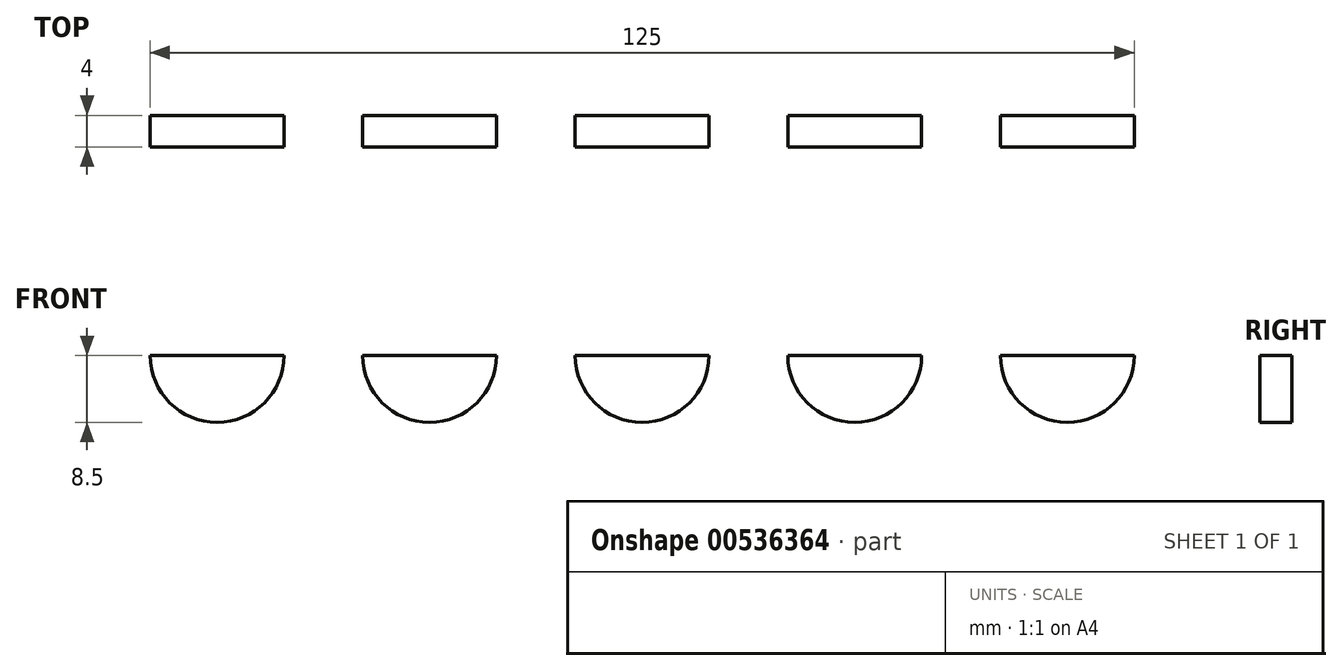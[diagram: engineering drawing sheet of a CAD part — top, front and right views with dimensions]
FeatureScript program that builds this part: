
annotation { "Feature Type Name" : "Feature", "Feature Type Description" : "" }
export const myFeature = defineFeature(function(context is Context, id is Id, definition is map)
    precondition{}
    {
        {
            var Q0;
            Q0=qCreatedBy(makeId("Front.planeOp"),FACE);
            var sketch = newSketch(context, id + "F0", { "sketchPlane" : qUnion([Q0])});
            skLineSegment(sketch, "E0.bottom", {"start": v(-72.5, 7.5) * mm, "end": v(72.5, 7.5) * mm});
            skLineSegment(sketch, "E0.top", {"start": v(-72.5, -7.5) * mm, "end": v(72.5, -7.5) * mm});
            skLineSegment(sketch, "E0.left", {"start": v(-72.5, 7.5) * mm, "end": v(-72.5, -7.5) * mm});
            skLineSegment(sketch, "E0.right", {"start": v(72.5, 7.5) * mm, "end": v(72.5, -7.5) * mm});
            skPoint(sketch, "E0.middle", {"position": v(0, 0) * mm});
            skLineSegment(sketch, "E1", {"start": v(-72.5, 7.5) * mm, "end": v(-62.5, 7.5) * mm});
            skLineSegment(sketch, "E2", {"start": v(-62.5, 7.5) * mm, "end": v(-54, 7.5) * mm});
            skLineSegment(sketch, "E3", {"start": v(-54, 7.5) * mm, "end": v(-45.5, 7.5) * mm});
            skLineSegment(sketch, "E4", {"start": v(-45.5, 7.5) * mm, "end": v(-35.5, 7.5) * mm});
            skLineSegment(sketch, "E5", {"start": v(-35.5, 7.5) * mm, "end": v(-27, 7.5) * mm});
            skLineSegment(sketch, "E6", {"start": v(-27, 7.5) * mm, "end": v(-18.5, 7.5) * mm});
            skLineSegment(sketch, "E7", {"start": v(-18.5, 7.5) * mm, "end": v(-8.5, 7.5) * mm});
            skLineSegment(sketch, "E8", {"start": v(-8.5, 7.5) * mm, "end": v(0, 7.5) * mm});
            skLineSegment(sketch, "E9", {"start": v(0, 7.5) * mm, "end": v(8.5, 7.5) * mm});
            skLineSegment(sketch, "E10", {"start": v(8.5, 7.5) * mm, "end": v(18.5, 7.5) * mm});
            skLineSegment(sketch, "E11", {"start": v(18.5, 7.5) * mm, "end": v(27, 7.5) * mm});
            skLineSegment(sketch, "E12", {"start": v(27, 7.5) * mm, "end": v(35.5, 7.5) * mm});
            skLineSegment(sketch, "E13", {"start": v(35.5, 7.5) * mm, "end": v(45.5, 7.5) * mm});
            skLineSegment(sketch, "E14", {"start": v(45.5, 7.5) * mm, "end": v(54, 7.5) * mm});
            skLineSegment(sketch, "E15", {"start": v(54, 7.5) * mm, "end": v(62.5, 7.5) * mm});
            skCircle(sketch, "E16", {"center": v(-54, 7.5) * mm, "radius": 8.5 * mm});
            skCircle(sketch, "E17", {"center": v(-27, 7.5) * mm, "radius": 8.5 * mm});
            skCircle(sketch, "E18", {"center": v(0, 7.5) * mm, "radius": 8.5 * mm});
            skCircle(sketch, "E19", {"center": v(27, 7.5) * mm, "radius": 8.5 * mm});
            skCircle(sketch, "E20", {"center": v(54, 7.5) * mm, "radius": 8.5 * mm});
            skLineSegment(sketch, "E21", {"start": v(-72.5, -7.5) * mm, "end": v(-57.5, -7.5) * mm});
            skLineSegment(sketch, "E22", {"start": v(-57.5, -7.5) * mm, "end": v(-57.5, -3.5) * mm});
            skLineSegment(sketch, "E23", {"start": v(-57.5, -3.5) * mm, "end": v(-72.5, -3.5) * mm});
            skLineSegment(sketch, "E24", {"start": v(-72.5, -3.5) * mm, "end": v(-72.5, -7.5) * mm});
            skLineSegment(sketch, "E25", {"start": v(-57.5, -7.5) * mm, "end": v(-42.5, -7.5) * mm});
            skLineSegment(sketch, "E26", {"start": v(-42.5, -7.5) * mm, "end": v(-42.5, -3.5) * mm});
            skLineSegment(sketch, "E27", {"start": v(-42.5, -3.5) * mm, "end": v(-7.5, -3.5) * mm});
            skLineSegment(sketch, "E28", {"start": v(-7.5, -3.5) * mm, "end": v(-7.5, -7.5) * mm});
            skLineSegment(sketch, "E29", {"start": v(-7.5, -7.5) * mm, "end": v(7.5, -7.5) * mm});
            skLineSegment(sketch, "E30", {"start": v(7.5, -7.5) * mm, "end": v(7.5, -3.5) * mm});
            skLineSegment(sketch, "E31", {"start": v(7.5, -3.5) * mm, "end": v(42.5, -3.5) * mm});
            skLineSegment(sketch, "E32", {"start": v(42.5, -3.5) * mm, "end": v(42.5, -7.5) * mm});
            skLineSegment(sketch, "E33", {"start": v(42.5, -7.5) * mm, "end": v(57.5, -7.5) * mm});
            skLineSegment(sketch, "E34", {"start": v(57.5, -7.5) * mm, "end": v(57.5, -3.5) * mm});
            skLineSegment(sketch, "E35", {"start": v(72.5, -7.5) * mm, "end": v(72.5, -3.5) * mm});
            skLineSegment(sketch, "E36", {"start": v(72.5, -3.5) * mm, "end": v(57.5, -3.5) * mm});
            skSolve(sketch);
        }
        {
            var Q0;
            {var subQ1=sQuery(id+"F0.wireOp",EDGE,"E0.bottom");Q0=makeQuery(id+"F0.imprint","IMPRINT",FACE,{"disambiguationData":[TD([[makeQuery(id+"F0.imprint","IMPRINT",EDGE,{"derivedFrom":subQ1}),-1.0]])]});}
            extrude(context, id + "F1", {"entities" : qUnion([Q0]), "depth" : 4 * mm, "offsetDistance" : 25 * mm});
        }
    });
